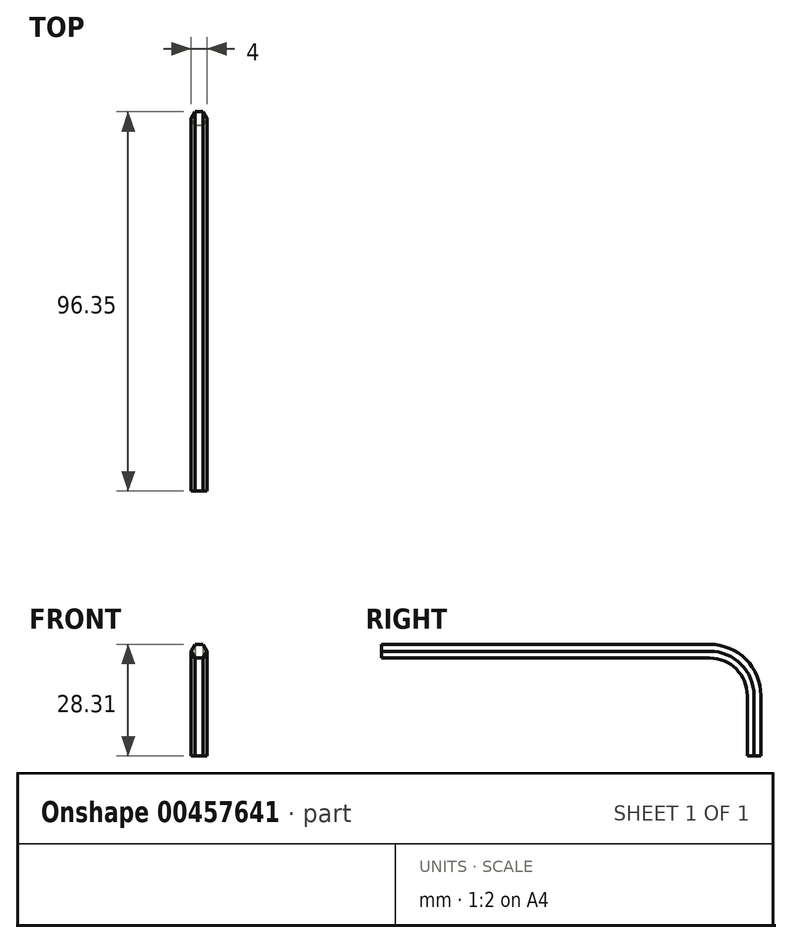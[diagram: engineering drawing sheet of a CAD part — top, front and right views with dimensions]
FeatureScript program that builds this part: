
annotation { "Feature Type Name" : "Feature", "Feature Type Description" : "" }
export const myFeature = defineFeature(function(context is Context, id is Id, definition is map)
    precondition{}
    {
        {
            var Q0;
            Q0=qCreatedBy(makeId("Front.planeOp"),FACE);
            var sketch = newSketch(context, id + "F0", { "sketchPlane" : qUnion([Q0])});
            skCircle(sketch, "E0.cCircle", {"center": v(0, 0) * mm, "radius": 1.73 * mm, "construction": true});
            skLineSegment(sketch, "E0.0", {"start": v(1, -1.73) * mm, "end": v(-1, -1.73) * mm});
            skLineSegment(sketch, "E0.1", {"start": v(-1, -1.73) * mm, "end": v(-2, 0) * mm});
            skLineSegment(sketch, "E0.2", {"start": v(-2, 0) * mm, "end": v(-1, 1.73) * mm});
            skLineSegment(sketch, "E0.3", {"start": v(-1, 1.73) * mm, "end": v(1, 1.73) * mm});
            skLineSegment(sketch, "E0.4", {"start": v(1, 1.73) * mm, "end": v(2, 0) * mm});
            skLineSegment(sketch, "E0.5", {"start": v(2, 0) * mm, "end": v(1, -1.73) * mm});
            skPoint(sketch, "E0.0.midPoint", {"position": v(0, -1.73) * mm});
            skSolve(sketch);
        }
        {
            var Q0;
            Q0=qCreatedBy(makeId("Right.planeOp"),FACE);
            var sketch = newSketch(context, id + "F1", { "sketchPlane" : qUnion([Q0])});
            skLineSegment(sketch, "E1", {"start": v(99.84, -26.58) * mm, "end": v(99.84, -11.28) * mm});
            skLineSegment(sketch, "E2", {"start": v(83.33, 5.23) * mm, "end": v(0, 5.23) * mm});
            skPoint(sketch, "E3.visualSharp", {"position": v(99.84, 5.23) * mm});
            skArc(sketch, "E3.filletArc", {"start": v(99.84, -11.28) * mm, "mid": v(95, 0.4) * mm, "end": v(83.33, 5.23) * mm});
            skSolve(sketch);
        }
        {
            var Q0;
            Q0=makeQuery(id+"F0.imprint","IMPRINT",FACE,{"disambiguationData":[TD([[makeQuery(id+"F0.imprint","IMPRINT",EDGE,{"derivedFrom":sQuery(id+"F0.wireOp",EDGE,"E0.0")}),-1.0]])]});
            var Q1;
            Q1=sQuery(id+"F1.wireOp",EDGE,"E2");
            var Q2;
            Q2=sQuery(id+"F1.wireOp",EDGE,"E3.filletArc");
            var Q3;
            Q3=sQuery(id+"F1.wireOp",EDGE,"E1");
            sweep(context, id + "F2", {"profiles" : qUnion([Q0]), "path" : qUnion([Q1, Q2, Q3])});
        }
    });
